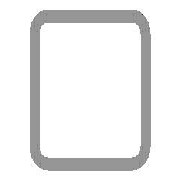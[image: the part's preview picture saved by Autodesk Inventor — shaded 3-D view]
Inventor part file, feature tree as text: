
AUTODESK INVENTOR PART (.ipt)
format: ipt  version: 2025 (Build 290162010, 162A)  size: 143,872 bytes
history: native  units: mm (DEFAULTED — no unit token found)
features: other x4, plane x2, split x1, sketch x1
ambient origin geometry x8: Origin, YZ Plane, XZ Plane, XY Plane, X Axis, Y Axis, Z Axis, Center Point
bodies: Solid1 (feature_tree), Body (feature_tree)
feature tree (8):
  parser-record x1  (decoder bookkeeping rows leaked as tree rows — omitted from the tree; the rows remain in map.json)
  other  "Driven Length"
  other  "Start Plane"
  other  "End Plane"
  plane  "Work Plane4"
  split  "Split1"
  sketch  "Sketch3"  dims[d3=626.129918mm d4=0.0mm d7=6.0mm d9=60.0mm d11=60.0mm d12=3.0mm d13=100.0mm d14=726.129918mm d15=30.0mm d16=30.0mm d17=90.0deg d18=626.129918mm]
  plane  "Work Plane3"
